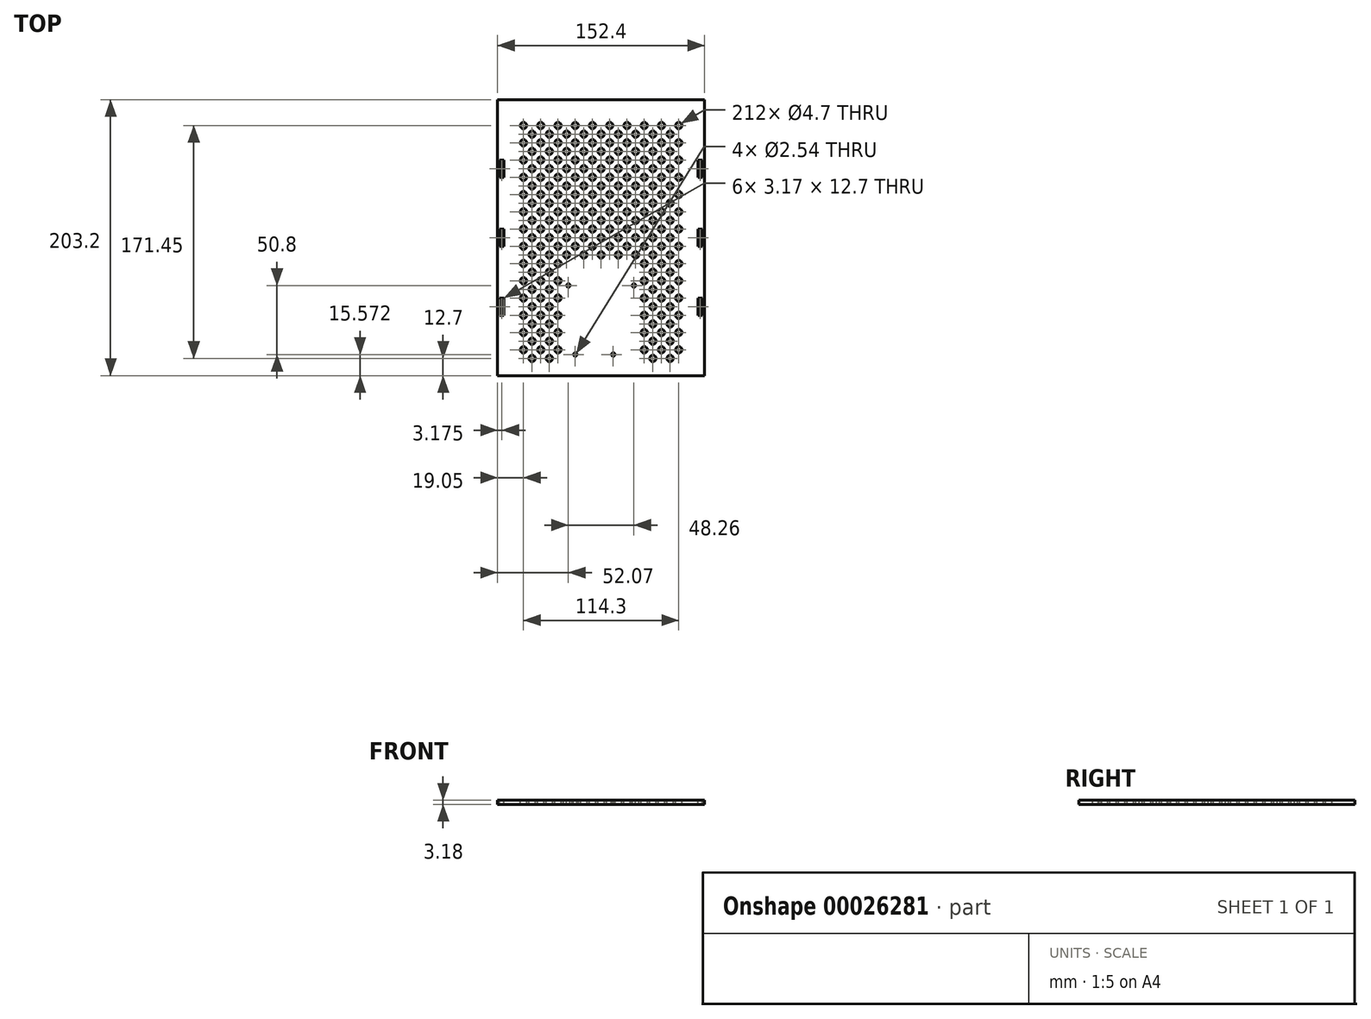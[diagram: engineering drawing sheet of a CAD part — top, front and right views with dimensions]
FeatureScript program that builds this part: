
annotation { "Feature Type Name" : "Feature", "Feature Type Description" : "" }
export const myFeature = defineFeature(function(context is Context, id is Id, definition is map)
    precondition{}
    {
        {
            var Q0;
            Q0=qCreatedBy(makeId("Top.planeOp"),FACE);
            var sketch = newSketch(context, id + "F0", { "sketchPlane" : qUnion([Q0])});
            skLineSegment(sketch, "E0.rect.bottom", {"start": v(76.2, -101.6) * mm, "end": v(-76.2, -101.6) * mm});
            skLineSegment(sketch, "E0.rect.top", {"start": v(76.2, 101.6) * mm, "end": v(-76.2, 101.6) * mm});
            skLineSegment(sketch, "E0.rect.left", {"start": v(76.2, -101.6) * mm, "end": v(76.2, 101.6) * mm});
            skLineSegment(sketch, "E0.rect.right", {"start": v(-76.2, -101.6) * mm, "end": v(-76.2, 101.6) * mm});
            skPoint(sketch, "E0.rect.middle", {"position": v(0, 0) * mm});
            skCircle(sketch, "E1", {"center": v(-57.15, 82.55) * mm, "radius": 2.35 * mm});
            skCircle(sketch, "E2.1.0.0", {"center": v(-44.45, 82.55) * mm, "radius": 2.35 * mm});
            skCircle(sketch, "E2.2.0.0", {"center": v(-31.75, 82.55) * mm, "radius": 2.35 * mm});
            skCircle(sketch, "E2.3.0.0", {"center": v(-19.05, 82.55) * mm, "radius": 2.35 * mm});
            skCircle(sketch, "E2.4.0.0", {"center": v(-6.35, 82.55) * mm, "radius": 2.35 * mm});
            skCircle(sketch, "E2.5.0.0", {"center": v(6.35, 82.55) * mm, "radius": 2.35 * mm});
            skCircle(sketch, "E2.6.0.0", {"center": v(19.05, 82.55) * mm, "radius": 2.35 * mm});
            skCircle(sketch, "E2.7.0.0", {"center": v(31.75, 82.55) * mm, "radius": 2.35 * mm});
            skCircle(sketch, "E2.8.0.0", {"center": v(44.45, 82.55) * mm, "radius": 2.35 * mm});
            skCircle(sketch, "E2.9.0.0", {"center": v(57.15, 82.55) * mm, "radius": 2.35 * mm});
            skLineSegment(sketch, "E2.direction1", {"start": v(-57.15, 82.55) * mm, "end": v(-44.45, 82.55) * mm, "construction": true});
            skCircle(sketch, "E3.0.1.0", {"center": v(-57.15, 69.85) * mm, "radius": 2.35 * mm});
            skCircle(sketch, "E3.0.2.0", {"center": v(-57.15, 57.15) * mm, "radius": 2.35 * mm});
            skCircle(sketch, "E3.0.3.0", {"center": v(-57.15, 44.45) * mm, "radius": 2.35 * mm});
            skCircle(sketch, "E3.0.4.0", {"center": v(-57.15, 31.75) * mm, "radius": 2.35 * mm});
            skCircle(sketch, "E3.0.5.0", {"center": v(-57.15, 19.05) * mm, "radius": 2.35 * mm});
            skCircle(sketch, "E3.0.6.0", {"center": v(-57.15, 6.35) * mm, "radius": 2.35 * mm});
            skCircle(sketch, "E3.0.7.0", {"center": v(-57.15, -6.35) * mm, "radius": 2.35 * mm});
            skCircle(sketch, "E3.0.8.0", {"center": v(-57.15, -19.05) * mm, "radius": 2.35 * mm});
            skCircle(sketch, "E3.0.9.0", {"center": v(-57.15, -31.75) * mm, "radius": 2.35 * mm});
            skCircle(sketch, "E3.1.1.0", {"center": v(-44.45, 69.85) * mm, "radius": 2.35 * mm});
            skCircle(sketch, "E3.1.2.0", {"center": v(-44.45, 57.15) * mm, "radius": 2.35 * mm});
            skCircle(sketch, "E3.1.3.0", {"center": v(-44.45, 44.45) * mm, "radius": 2.35 * mm});
            skCircle(sketch, "E3.1.4.0", {"center": v(-44.45, 31.75) * mm, "radius": 2.35 * mm});
            skCircle(sketch, "E3.1.5.0", {"center": v(-44.45, 19.05) * mm, "radius": 2.35 * mm});
            skCircle(sketch, "E3.1.6.0", {"center": v(-44.45, 6.35) * mm, "radius": 2.35 * mm});
            skCircle(sketch, "E3.1.7.0", {"center": v(-44.45, -6.35) * mm, "radius": 2.35 * mm});
            skCircle(sketch, "E3.1.8.0", {"center": v(-44.45, -19.05) * mm, "radius": 2.35 * mm});
            skCircle(sketch, "E3.1.9.0", {"center": v(-44.45, -31.75) * mm, "radius": 2.35 * mm});
            skCircle(sketch, "E3.2.1.0", {"center": v(-31.75, 69.85) * mm, "radius": 2.35 * mm});
            skCircle(sketch, "E3.2.2.0", {"center": v(-31.75, 57.15) * mm, "radius": 2.35 * mm});
            skCircle(sketch, "E3.2.3.0", {"center": v(-31.75, 44.45) * mm, "radius": 2.35 * mm});
            skCircle(sketch, "E3.2.4.0", {"center": v(-31.75, 31.75) * mm, "radius": 2.35 * mm});
            skCircle(sketch, "E3.2.5.0", {"center": v(-31.75, 19.05) * mm, "radius": 2.35 * mm});
            skCircle(sketch, "E3.2.6.0", {"center": v(-31.75, 6.35) * mm, "radius": 2.35 * mm});
            skCircle(sketch, "E3.2.7.0", {"center": v(-31.75, -6.35) * mm, "radius": 2.35 * mm});
            skCircle(sketch, "E3.2.8.0", {"center": v(-31.75, -19.05) * mm, "radius": 2.35 * mm});
            skCircle(sketch, "E3.2.9.0", {"center": v(-31.75, -31.75) * mm, "radius": 2.35 * mm});
            skCircle(sketch, "E3.3.1.0", {"center": v(-19.05, 69.85) * mm, "radius": 2.35 * mm});
            skCircle(sketch, "E3.3.2.0", {"center": v(-19.05, 57.15) * mm, "radius": 2.35 * mm});
            skCircle(sketch, "E3.3.3.0", {"center": v(-19.05, 44.45) * mm, "radius": 2.35 * mm});
            skCircle(sketch, "E3.3.4.0", {"center": v(-19.05, 31.75) * mm, "radius": 2.35 * mm});
            skCircle(sketch, "E3.3.5.0", {"center": v(-19.05, 19.05) * mm, "radius": 2.35 * mm});
            skCircle(sketch, "E3.3.6.0", {"center": v(-19.05, 6.35) * mm, "radius": 2.35 * mm});
            skCircle(sketch, "E3.3.7.0", {"center": v(-19.05, -6.35) * mm, "radius": 2.35 * mm});
            skCircle(sketch, "E3.4.1.0", {"center": v(-6.35, 69.85) * mm, "radius": 2.35 * mm});
            skCircle(sketch, "E3.4.2.0", {"center": v(-6.35, 57.15) * mm, "radius": 2.35 * mm});
            skCircle(sketch, "E3.4.3.0", {"center": v(-6.35, 44.45) * mm, "radius": 2.35 * mm});
            skCircle(sketch, "E3.4.4.0", {"center": v(-6.35, 31.75) * mm, "radius": 2.35 * mm});
            skCircle(sketch, "E3.4.5.0", {"center": v(-6.35, 19.05) * mm, "radius": 2.35 * mm});
            skCircle(sketch, "E3.4.6.0", {"center": v(-6.35, 6.35) * mm, "radius": 2.35 * mm});
            skCircle(sketch, "E3.4.7.0", {"center": v(-6.35, -6.35) * mm, "radius": 2.35 * mm});
            skCircle(sketch, "E3.5.1.0", {"center": v(6.35, 69.85) * mm, "radius": 2.35 * mm});
            skCircle(sketch, "E3.5.2.0", {"center": v(6.35, 57.15) * mm, "radius": 2.35 * mm});
            skCircle(sketch, "E3.5.3.0", {"center": v(6.35, 44.45) * mm, "radius": 2.35 * mm});
            skCircle(sketch, "E3.5.4.0", {"center": v(6.35, 31.75) * mm, "radius": 2.35 * mm});
            skCircle(sketch, "E3.5.5.0", {"center": v(6.35, 19.05) * mm, "radius": 2.35 * mm});
            skCircle(sketch, "E3.5.6.0", {"center": v(6.35, 6.35) * mm, "radius": 2.35 * mm});
            skCircle(sketch, "E3.5.7.0", {"center": v(6.35, -6.35) * mm, "radius": 2.35 * mm});
            skCircle(sketch, "E3.6.1.0", {"center": v(19.05, 69.85) * mm, "radius": 2.35 * mm});
            skCircle(sketch, "E3.6.2.0", {"center": v(19.05, 57.15) * mm, "radius": 2.35 * mm});
            skCircle(sketch, "E3.6.3.0", {"center": v(19.05, 44.45) * mm, "radius": 2.35 * mm});
            skCircle(sketch, "E3.6.4.0", {"center": v(19.05, 31.75) * mm, "radius": 2.35 * mm});
            skCircle(sketch, "E3.6.5.0", {"center": v(19.05, 19.05) * mm, "radius": 2.35 * mm});
            skCircle(sketch, "E3.6.6.0", {"center": v(19.05, 6.35) * mm, "radius": 2.35 * mm});
            skCircle(sketch, "E3.6.7.0", {"center": v(19.05, -6.35) * mm, "radius": 2.35 * mm});
            skCircle(sketch, "E3.7.1.0", {"center": v(31.75, 69.85) * mm, "radius": 2.35 * mm});
            skCircle(sketch, "E3.7.2.0", {"center": v(31.75, 57.15) * mm, "radius": 2.35 * mm});
            skCircle(sketch, "E3.7.3.0", {"center": v(31.75, 44.45) * mm, "radius": 2.35 * mm});
            skCircle(sketch, "E3.7.4.0", {"center": v(31.75, 31.75) * mm, "radius": 2.35 * mm});
            skCircle(sketch, "E3.7.5.0", {"center": v(31.75, 19.05) * mm, "radius": 2.35 * mm});
            skCircle(sketch, "E3.7.6.0", {"center": v(31.75, 6.35) * mm, "radius": 2.35 * mm});
            skCircle(sketch, "E3.7.7.0", {"center": v(31.75, -6.35) * mm, "radius": 2.35 * mm});
            skCircle(sketch, "E3.7.8.0", {"center": v(31.75, -19.05) * mm, "radius": 2.35 * mm});
            skCircle(sketch, "E3.7.9.0", {"center": v(31.75, -31.75) * mm, "radius": 2.35 * mm});
            skCircle(sketch, "E3.8.1.0", {"center": v(44.45, 69.85) * mm, "radius": 2.35 * mm});
            skCircle(sketch, "E3.8.2.0", {"center": v(44.45, 57.15) * mm, "radius": 2.35 * mm});
            skCircle(sketch, "E3.8.3.0", {"center": v(44.45, 44.45) * mm, "radius": 2.35 * mm});
            skCircle(sketch, "E3.8.4.0", {"center": v(44.45, 31.75) * mm, "radius": 2.35 * mm});
            skCircle(sketch, "E3.8.5.0", {"center": v(44.45, 19.05) * mm, "radius": 2.35 * mm});
            skCircle(sketch, "E3.8.6.0", {"center": v(44.45, 6.35) * mm, "radius": 2.35 * mm});
            skCircle(sketch, "E3.8.7.0", {"center": v(44.45, -6.35) * mm, "radius": 2.35 * mm});
            skCircle(sketch, "E3.8.8.0", {"center": v(44.45, -19.05) * mm, "radius": 2.35 * mm});
            skCircle(sketch, "E3.8.9.0", {"center": v(44.45, -31.75) * mm, "radius": 2.35 * mm});
            skCircle(sketch, "E3.9.1.0", {"center": v(57.15, 69.85) * mm, "radius": 2.35 * mm});
            skCircle(sketch, "E3.9.2.0", {"center": v(57.15, 57.15) * mm, "radius": 2.35 * mm});
            skCircle(sketch, "E3.9.3.0", {"center": v(57.15, 44.45) * mm, "radius": 2.35 * mm});
            skCircle(sketch, "E3.9.4.0", {"center": v(57.15, 31.75) * mm, "radius": 2.35 * mm});
            skCircle(sketch, "E3.9.5.0", {"center": v(57.15, 19.05) * mm, "radius": 2.35 * mm});
            skCircle(sketch, "E3.9.6.0", {"center": v(57.15, 6.35) * mm, "radius": 2.35 * mm});
            skCircle(sketch, "E3.9.7.0", {"center": v(57.15, -6.35) * mm, "radius": 2.35 * mm});
            skCircle(sketch, "E3.9.8.0", {"center": v(57.15, -19.05) * mm, "radius": 2.35 * mm});
            skCircle(sketch, "E3.9.9.0", {"center": v(57.15, -31.75) * mm, "radius": 2.35 * mm});
            skLineSegment(sketch, "E3.direction2", {"start": v(-57.15, 82.55) * mm, "end": v(-57.15, 69.85) * mm, "construction": true});
            skCircle(sketch, "E4.0.1.0", {"center": v(-57.15, -44.45) * mm, "radius": 2.35 * mm});
            skCircle(sketch, "E4.0.2.0", {"center": v(-57.15, -57.15) * mm, "radius": 2.35 * mm});
            skCircle(sketch, "E4.0.3.0", {"center": v(-57.15, -69.85) * mm, "radius": 2.35 * mm});
            skCircle(sketch, "E4.0.4.0", {"center": v(-57.15, -82.55) * mm, "radius": 2.35 * mm});
            skCircle(sketch, "E4.1.1.0", {"center": v(-44.45, -44.45) * mm, "radius": 2.35 * mm});
            skCircle(sketch, "E4.1.2.0", {"center": v(-44.45, -57.15) * mm, "radius": 2.35 * mm});
            skCircle(sketch, "E4.1.3.0", {"center": v(-44.45, -69.85) * mm, "radius": 2.35 * mm});
            skCircle(sketch, "E4.1.4.0", {"center": v(-44.45, -82.55) * mm, "radius": 2.35 * mm});
            skCircle(sketch, "E4.2.1.0", {"center": v(-31.75, -44.45) * mm, "radius": 2.35 * mm});
            skCircle(sketch, "E4.2.2.0", {"center": v(-31.75, -57.15) * mm, "radius": 2.35 * mm});
            skCircle(sketch, "E4.2.3.0", {"center": v(-31.75, -69.85) * mm, "radius": 2.35 * mm});
            skCircle(sketch, "E4.2.4.0", {"center": v(-31.75, -82.55) * mm, "radius": 2.35 * mm});
            skCircle(sketch, "E4.7.1.0", {"center": v(31.75, -44.45) * mm, "radius": 2.35 * mm});
            skCircle(sketch, "E4.7.2.0", {"center": v(31.75, -57.15) * mm, "radius": 2.35 * mm});
            skCircle(sketch, "E4.7.3.0", {"center": v(31.75, -69.85) * mm, "radius": 2.35 * mm});
            skCircle(sketch, "E4.7.4.0", {"center": v(31.75, -82.55) * mm, "radius": 2.35 * mm});
            skCircle(sketch, "E4.8.1.0", {"center": v(44.45, -44.45) * mm, "radius": 2.35 * mm});
            skCircle(sketch, "E4.8.2.0", {"center": v(44.45, -57.15) * mm, "radius": 2.35 * mm});
            skCircle(sketch, "E4.8.3.0", {"center": v(44.45, -69.85) * mm, "radius": 2.35 * mm});
            skCircle(sketch, "E4.8.4.0", {"center": v(44.45, -82.55) * mm, "radius": 2.35 * mm});
            skCircle(sketch, "E4.9.1.0", {"center": v(57.15, -44.45) * mm, "radius": 2.35 * mm});
            skCircle(sketch, "E4.9.2.0", {"center": v(57.15, -57.15) * mm, "radius": 2.35 * mm});
            skCircle(sketch, "E4.9.3.0", {"center": v(57.15, -69.85) * mm, "radius": 2.35 * mm});
            skCircle(sketch, "E4.9.4.0", {"center": v(57.15, -82.55) * mm, "radius": 2.35 * mm});
            skLineSegment(sketch, "E4.direction1", {"start": v(-57.15, -31.75) * mm, "end": v(-44.45, -31.75) * mm, "construction": true});
            skLineSegment(sketch, "E4.direction2", {"start": v(-57.15, -31.75) * mm, "end": v(-57.15, -44.45) * mm, "construction": true});
            skPoint(sketch, "E5", {"position": v(-73.03, 50.8) * mm});
            skPoint(sketch, "E6", {"position": v(-73.03, 0) * mm});
            skPoint(sketch, "E7", {"position": v(-73.03, -50.8) * mm});
            skCircle(sketch, "E8", {"center": v(-50.8, 76.2) * mm, "radius": 2.35 * mm});
            skCircle(sketch, "E9.0.1.0", {"center": v(-50.8, 63.5) * mm, "radius": 2.35 * mm});
            skCircle(sketch, "E9.0.2.0", {"center": v(-50.8, 50.8) * mm, "radius": 2.35 * mm});
            skCircle(sketch, "E9.0.3.0", {"center": v(-50.8, 38.1) * mm, "radius": 2.35 * mm});
            skCircle(sketch, "E9.0.4.0", {"center": v(-50.8, 25.4) * mm, "radius": 2.35 * mm});
            skCircle(sketch, "E9.0.5.0", {"center": v(-50.8, 12.7) * mm, "radius": 2.35 * mm});
            skCircle(sketch, "E9.0.6.0", {"center": v(-50.8, 0) * mm, "radius": 2.35 * mm});
            skCircle(sketch, "E9.0.7.0", {"center": v(-50.8, -12.7) * mm, "radius": 2.35 * mm});
            skCircle(sketch, "E9.0.8.0", {"center": v(-50.8, -25.4) * mm, "radius": 2.35 * mm});
            skCircle(sketch, "E9.1.0.0", {"center": v(-38.1, 76.2) * mm, "radius": 2.35 * mm});
            skCircle(sketch, "E9.1.1.0", {"center": v(-38.1, 63.5) * mm, "radius": 2.35 * mm});
            skCircle(sketch, "E9.1.2.0", {"center": v(-38.1, 50.8) * mm, "radius": 2.35 * mm});
            skCircle(sketch, "E9.1.3.0", {"center": v(-38.1, 38.1) * mm, "radius": 2.35 * mm});
            skCircle(sketch, "E9.1.4.0", {"center": v(-38.1, 25.4) * mm, "radius": 2.35 * mm});
            skCircle(sketch, "E9.1.5.0", {"center": v(-38.1, 12.7) * mm, "radius": 2.35 * mm});
            skCircle(sketch, "E9.1.6.0", {"center": v(-38.1, 0) * mm, "radius": 2.35 * mm});
            skCircle(sketch, "E9.1.7.0", {"center": v(-38.1, -12.7) * mm, "radius": 2.35 * mm});
            skCircle(sketch, "E9.1.8.0", {"center": v(-38.1, -25.4) * mm, "radius": 2.35 * mm});
            skCircle(sketch, "E9.2.0.0", {"center": v(-25.4, 76.2) * mm, "radius": 2.35 * mm});
            skCircle(sketch, "E9.2.1.0", {"center": v(-25.4, 63.5) * mm, "radius": 2.35 * mm});
            skCircle(sketch, "E9.2.2.0", {"center": v(-25.4, 50.8) * mm, "radius": 2.35 * mm});
            skCircle(sketch, "E9.2.3.0", {"center": v(-25.4, 38.1) * mm, "radius": 2.35 * mm});
            skCircle(sketch, "E9.2.4.0", {"center": v(-25.4, 25.4) * mm, "radius": 2.35 * mm});
            skCircle(sketch, "E9.2.5.0", {"center": v(-25.4, 12.7) * mm, "radius": 2.35 * mm});
            skCircle(sketch, "E9.2.6.0", {"center": v(-25.4, 0) * mm, "radius": 2.35 * mm});
            skCircle(sketch, "E9.2.7.0", {"center": v(-25.4, -12.7) * mm, "radius": 2.35 * mm});
            skCircle(sketch, "E9.3.0.0", {"center": v(-12.7, 76.2) * mm, "radius": 2.35 * mm});
            skCircle(sketch, "E9.3.1.0", {"center": v(-12.7, 63.5) * mm, "radius": 2.35 * mm});
            skCircle(sketch, "E9.3.2.0", {"center": v(-12.7, 50.8) * mm, "radius": 2.35 * mm});
            skCircle(sketch, "E9.3.3.0", {"center": v(-12.7, 38.1) * mm, "radius": 2.35 * mm});
            skCircle(sketch, "E9.3.4.0", {"center": v(-12.7, 25.4) * mm, "radius": 2.35 * mm});
            skCircle(sketch, "E9.3.5.0", {"center": v(-12.7, 12.7) * mm, "radius": 2.35 * mm});
            skCircle(sketch, "E9.3.6.0", {"center": v(-12.7, 0) * mm, "radius": 2.35 * mm});
            skCircle(sketch, "E9.3.7.0", {"center": v(-12.7, -12.7) * mm, "radius": 2.35 * mm});
            skCircle(sketch, "E9.4.0.0", {"center": v(0, 76.2) * mm, "radius": 2.35 * mm});
            skCircle(sketch, "E9.4.1.0", {"center": v(0, 63.5) * mm, "radius": 2.35 * mm});
            skCircle(sketch, "E9.4.2.0", {"center": v(0, 50.8) * mm, "radius": 2.35 * mm});
            skCircle(sketch, "E9.4.3.0", {"center": v(0, 38.1) * mm, "radius": 2.35 * mm});
            skCircle(sketch, "E9.4.4.0", {"center": v(0, 25.4) * mm, "radius": 2.35 * mm});
            skCircle(sketch, "E9.4.5.0", {"center": v(0, 12.7) * mm, "radius": 2.35 * mm});
            skCircle(sketch, "E9.4.6.0", {"center": v(0, 0) * mm, "radius": 2.35 * mm});
            skCircle(sketch, "E9.4.7.0", {"center": v(0, -12.7) * mm, "radius": 2.35 * mm});
            skCircle(sketch, "E9.5.0.0", {"center": v(12.7, 76.2) * mm, "radius": 2.35 * mm});
            skCircle(sketch, "E9.5.1.0", {"center": v(12.7, 63.5) * mm, "radius": 2.35 * mm});
            skCircle(sketch, "E9.5.2.0", {"center": v(12.7, 50.8) * mm, "radius": 2.35 * mm});
            skCircle(sketch, "E9.5.3.0", {"center": v(12.7, 38.1) * mm, "radius": 2.35 * mm});
            skCircle(sketch, "E9.5.4.0", {"center": v(12.7, 25.4) * mm, "radius": 2.35 * mm});
            skCircle(sketch, "E9.5.5.0", {"center": v(12.7, 12.7) * mm, "radius": 2.35 * mm});
            skCircle(sketch, "E9.5.6.0", {"center": v(12.7, 0) * mm, "radius": 2.35 * mm});
            skCircle(sketch, "E9.5.7.0", {"center": v(12.7, -12.7) * mm, "radius": 2.35 * mm});
            skCircle(sketch, "E9.6.0.0", {"center": v(25.4, 76.2) * mm, "radius": 2.35 * mm});
            skCircle(sketch, "E9.6.1.0", {"center": v(25.4, 63.5) * mm, "radius": 2.35 * mm});
            skCircle(sketch, "E9.6.2.0", {"center": v(25.4, 50.8) * mm, "radius": 2.35 * mm});
            skCircle(sketch, "E9.6.3.0", {"center": v(25.4, 38.1) * mm, "radius": 2.35 * mm});
            skCircle(sketch, "E9.6.4.0", {"center": v(25.4, 25.4) * mm, "radius": 2.35 * mm});
            skCircle(sketch, "E9.6.5.0", {"center": v(25.4, 12.7) * mm, "radius": 2.35 * mm});
            skCircle(sketch, "E9.6.6.0", {"center": v(25.4, 0) * mm, "radius": 2.35 * mm});
            skCircle(sketch, "E9.6.7.0", {"center": v(25.4, -12.7) * mm, "radius": 2.35 * mm});
            skCircle(sketch, "E9.7.0.0", {"center": v(38.1, 76.2) * mm, "radius": 2.35 * mm});
            skCircle(sketch, "E9.7.1.0", {"center": v(38.1, 63.5) * mm, "radius": 2.35 * mm});
            skCircle(sketch, "E9.7.2.0", {"center": v(38.1, 50.8) * mm, "radius": 2.35 * mm});
            skCircle(sketch, "E9.7.3.0", {"center": v(38.1, 38.1) * mm, "radius": 2.35 * mm});
            skCircle(sketch, "E9.7.4.0", {"center": v(38.1, 25.4) * mm, "radius": 2.35 * mm});
            skCircle(sketch, "E9.7.5.0", {"center": v(38.1, 12.7) * mm, "radius": 2.35 * mm});
            skCircle(sketch, "E9.7.6.0", {"center": v(38.1, 0) * mm, "radius": 2.35 * mm});
            skCircle(sketch, "E9.7.7.0", {"center": v(38.1, -12.7) * mm, "radius": 2.35 * mm});
            skCircle(sketch, "E9.7.8.0", {"center": v(38.1, -25.4) * mm, "radius": 2.35 * mm});
            skCircle(sketch, "E9.8.0.0", {"center": v(50.8, 76.2) * mm, "radius": 2.35 * mm});
            skCircle(sketch, "E9.8.1.0", {"center": v(50.8, 63.5) * mm, "radius": 2.35 * mm});
            skCircle(sketch, "E9.8.2.0", {"center": v(50.8, 50.8) * mm, "radius": 2.35 * mm});
            skCircle(sketch, "E9.8.3.0", {"center": v(50.8, 38.1) * mm, "radius": 2.35 * mm});
            skCircle(sketch, "E9.8.4.0", {"center": v(50.8, 25.4) * mm, "radius": 2.35 * mm});
            skCircle(sketch, "E9.8.5.0", {"center": v(50.8, 12.7) * mm, "radius": 2.35 * mm});
            skCircle(sketch, "E9.8.6.0", {"center": v(50.8, 0) * mm, "radius": 2.35 * mm});
            skCircle(sketch, "E9.8.7.0", {"center": v(50.8, -12.7) * mm, "radius": 2.35 * mm});
            skCircle(sketch, "E9.8.8.0", {"center": v(50.8, -25.4) * mm, "radius": 2.35 * mm});
            skLineSegment(sketch, "E9.direction1", {"start": v(-50.8, 76.2) * mm, "end": v(-38.1, 76.2) * mm, "construction": true});
            skLineSegment(sketch, "E9.direction2", {"start": v(-50.8, 76.2) * mm, "end": v(-50.8, 63.5) * mm, "construction": true});
            skLineSegment(sketch, "E10", {"start": v(-57.15, -31.75) * mm, "end": v(-57.15, -44.45) * mm});
            skLineSegment(sketch, "E11", {"start": v(-57.15, -31.75) * mm, "end": v(-44.45, -31.75) * mm});
            skPoint(sketch, "E12", {"position": v(-50.8, -31.75) * mm});
            skPoint(sketch, "E13", {"position": v(-57.15, -38.1) * mm});
            skCircle(sketch, "E14", {"center": v(-50.8, -38.1) * mm, "radius": 2.35 * mm});
            skCircle(sketch, "E15.0.1.0", {"center": v(-50.8, -50.8) * mm, "radius": 2.35 * mm});
            skCircle(sketch, "E15.0.2.0", {"center": v(-50.8, -63.5) * mm, "radius": 2.35 * mm});
            skCircle(sketch, "E15.0.3.0", {"center": v(-50.8, -76.2) * mm, "radius": 2.35 * mm});
            skCircle(sketch, "E15.0.4.0", {"center": v(-50.8, -88.9) * mm, "radius": 2.35 * mm});
            skCircle(sketch, "E15.1.0.0", {"center": v(-38.1, -38.1) * mm, "radius": 2.35 * mm});
            skCircle(sketch, "E15.1.1.0", {"center": v(-38.1, -50.8) * mm, "radius": 2.35 * mm});
            skCircle(sketch, "E15.1.2.0", {"center": v(-38.1, -63.5) * mm, "radius": 2.35 * mm});
            skCircle(sketch, "E15.1.3.0", {"center": v(-38.1, -76.2) * mm, "radius": 2.35 * mm});
            skCircle(sketch, "E15.1.4.0", {"center": v(-38.1, -88.9) * mm, "radius": 2.35 * mm});
            skLineSegment(sketch, "E15.direction1", {"start": v(-50.8, -38.1) * mm, "end": v(-38.1, -38.1) * mm, "construction": true});
            skLineSegment(sketch, "E15.direction2", {"start": v(-50.8, -38.1) * mm, "end": v(-50.8, -50.8) * mm, "construction": true});
            skCircle(sketch, "E16", {"center": v(38.1, -38.1) * mm, "radius": 2.35 * mm});
            skCircle(sketch, "E17.0.1.0", {"center": v(38.1, -50.8) * mm, "radius": 2.35 * mm});
            skCircle(sketch, "E17.0.2.0", {"center": v(38.1, -63.5) * mm, "radius": 2.35 * mm});
            skCircle(sketch, "E17.0.3.0", {"center": v(38.1, -76.2) * mm, "radius": 2.35 * mm});
            skCircle(sketch, "E17.0.4.0", {"center": v(38.1, -88.9) * mm, "radius": 2.35 * mm});
            skCircle(sketch, "E17.1.0.0", {"center": v(50.8, -38.1) * mm, "radius": 2.35 * mm});
            skCircle(sketch, "E17.1.1.0", {"center": v(50.8, -50.8) * mm, "radius": 2.35 * mm});
            skCircle(sketch, "E17.1.2.0", {"center": v(50.8, -63.5) * mm, "radius": 2.35 * mm});
            skCircle(sketch, "E17.1.3.0", {"center": v(50.8, -76.2) * mm, "radius": 2.35 * mm});
            skCircle(sketch, "E17.1.4.0", {"center": v(50.8, -88.9) * mm, "radius": 2.35 * mm});
            skLineSegment(sketch, "E17.direction1", {"start": v(38.1, -38.1) * mm, "end": v(50.8, -38.1) * mm, "construction": true});
            skLineSegment(sketch, "E17.direction2", {"start": v(38.1, -38.1) * mm, "end": v(38.1, -50.8) * mm, "construction": true});
            skCircle(sketch, "E18", {"center": v(24.13, -35.23) * mm, "radius": 1.27 * mm});
            skCircle(sketch, "E19", {"center": v(-24.13, -35.23) * mm, "radius": 1.27 * mm});
            skCircle(sketch, "E20", {"center": v(8.9, -86.03) * mm, "radius": 1.27 * mm});
            skCircle(sketch, "E21", {"center": v(-19.05, -86.03) * mm, "radius": 1.27 * mm});
            skPoint(sketch, "E22", {"position": v(-73.03, 57.15) * mm});
            skPoint(sketch, "E23", {"position": v(-73.03, 44.45) * mm});
            skPoint(sketch, "E24", {"position": v(-74.61, 57.15) * mm});
            skPoint(sketch, "E25", {"position": v(-71.44, 57.15) * mm});
            skLineSegment(sketch, "E26.bottom", {"start": v(-74.61, 57.15) * mm, "end": v(-71.44, 57.15) * mm});
            skLineSegment(sketch, "E26.top", {"start": v(-74.61, 44.45) * mm, "end": v(-71.44, 44.45) * mm});
            skLineSegment(sketch, "E26.left", {"start": v(-74.61, 57.15) * mm, "end": v(-74.61, 44.45) * mm});
            skLineSegment(sketch, "E26.right", {"start": v(-71.44, 57.15) * mm, "end": v(-71.44, 44.45) * mm});
            skPoint(sketch, "E27", {"position": v(-73.03, 6.35) * mm});
            skPoint(sketch, "E28", {"position": v(-73.03, -6.35) * mm});
            skPoint(sketch, "E29", {"position": v(-74.61, 6.35) * mm});
            skPoint(sketch, "E30", {"position": v(-71.44, 6.35) * mm});
            skLineSegment(sketch, "E31.bottom", {"start": v(-74.61, 6.35) * mm, "end": v(-71.44, 6.35) * mm});
            skLineSegment(sketch, "E31.top", {"start": v(-74.61, -6.35) * mm, "end": v(-71.44, -6.35) * mm});
            skLineSegment(sketch, "E31.left", {"start": v(-74.61, 6.35) * mm, "end": v(-74.61, -6.35) * mm});
            skLineSegment(sketch, "E31.right", {"start": v(-71.44, 6.35) * mm, "end": v(-71.44, -6.35) * mm});
            skPoint(sketch, "E32", {"position": v(-73.03, -44.45) * mm});
            skPoint(sketch, "E33", {"position": v(-73.03, -57.15) * mm});
            skPoint(sketch, "E34", {"position": v(-74.61, -44.45) * mm});
            skPoint(sketch, "E35", {"position": v(-71.44, -44.45) * mm});
            skLineSegment(sketch, "E36.bottom", {"start": v(-74.61, -44.45) * mm, "end": v(-71.44, -44.45) * mm});
            skLineSegment(sketch, "E36.top", {"start": v(-74.61, -57.15) * mm, "end": v(-71.44, -57.15) * mm});
            skLineSegment(sketch, "E36.left", {"start": v(-74.61, -44.45) * mm, "end": v(-74.61, -57.15) * mm});
            skLineSegment(sketch, "E36.right", {"start": v(-71.44, -44.45) * mm, "end": v(-71.44, -57.15) * mm});
            skPoint(sketch, "E37", {"position": v(73.02, 50.8) * mm});
            skPoint(sketch, "E38", {"position": v(73.02, 0) * mm});
            skPoint(sketch, "E39", {"position": v(73.02, -50.8) * mm});
            skPoint(sketch, "E40", {"position": v(73.02, 57.15) * mm});
            skPoint(sketch, "E41", {"position": v(73.02, 44.45) * mm});
            skPoint(sketch, "E42", {"position": v(71.44, 57.15) * mm});
            skPoint(sketch, "E43", {"position": v(74.61, 57.15) * mm});
            skLineSegment(sketch, "E44.bottom", {"start": v(71.44, 57.15) * mm, "end": v(74.61, 57.15) * mm});
            skLineSegment(sketch, "E44.top", {"start": v(71.44, 44.45) * mm, "end": v(74.61, 44.45) * mm});
            skLineSegment(sketch, "E44.left", {"start": v(71.44, 57.15) * mm, "end": v(71.44, 44.45) * mm});
            skLineSegment(sketch, "E44.right", {"start": v(74.61, 57.15) * mm, "end": v(74.61, 44.45) * mm});
            skPoint(sketch, "E45", {"position": v(73.02, 6.35) * mm});
            skPoint(sketch, "E46", {"position": v(73.02, -6.35) * mm});
            skLineSegment(sketch, "E47.bottom", {"start": v(71.44, 6.35) * mm, "end": v(74.61, 6.35) * mm});
            skLineSegment(sketch, "E47.top", {"start": v(71.44, -6.35) * mm, "end": v(74.61, -6.35) * mm});
            skLineSegment(sketch, "E47.left", {"start": v(71.44, 6.35) * mm, "end": v(71.44, -6.35) * mm});
            skLineSegment(sketch, "E47.right", {"start": v(74.61, 6.35) * mm, "end": v(74.61, -6.35) * mm});
            skPoint(sketch, "E48", {"position": v(73.02, -44.45) * mm});
            skPoint(sketch, "E49", {"position": v(73.02, -57.15) * mm});
            skLineSegment(sketch, "E50.bottom", {"start": v(71.44, -44.45) * mm, "end": v(74.61, -44.45) * mm});
            skLineSegment(sketch, "E50.top", {"start": v(71.44, -57.15) * mm, "end": v(74.61, -57.15) * mm});
            skLineSegment(sketch, "E50.left", {"start": v(71.44, -44.45) * mm, "end": v(71.44, -57.15) * mm});
            skLineSegment(sketch, "E50.right", {"start": v(74.61, -44.45) * mm, "end": v(74.61, -57.15) * mm});
            skSolve(sketch);
        }
        {
            var Q0;
            Q0=makeQuery(id+"F0.imprint","IMPRINT",FACE,{"disambiguationData":[TD([[makeQuery(id+"F0.imprint","IMPRINT",EDGE,{"derivedFrom":sQuery(id+"F0.wireOp",EDGE,"E0.rect.bottom")}),-1.0]])]});
            extrude(context, id + "F1", {"entities" : qUnion([Q0]), "oppositeDirection" : true, "depth" : 3.17 * mm});
        }
        {
            var Q0;
            Q0=makeQuery(id+"F1.opExtrude","SWEPT_FACE",FACE,{"disambiguationData":[OSD([sQuery(id+"F0.wireOp",EDGE,"E0.rect.left")])]});
            cPlane(context, id + "F2", {"entities" : qUnion([Q0]), "cplaneType" : CPlaneType.OFFSET, "offset" : 0 * mm, "width" : 152.4 * mm, "height" : 152.4 * mm});
        }
    });
